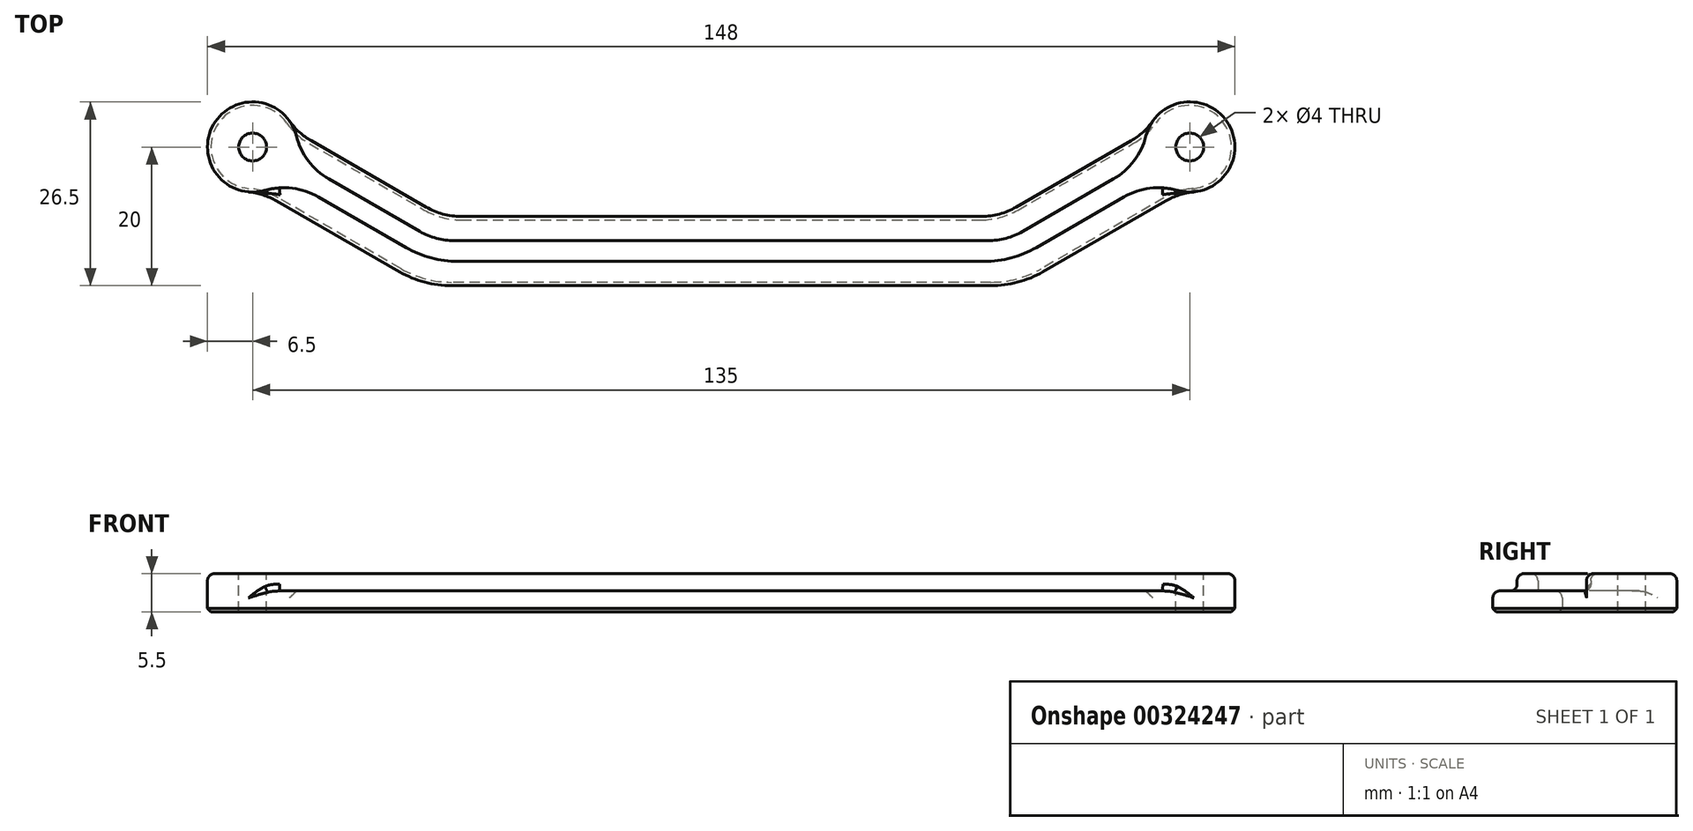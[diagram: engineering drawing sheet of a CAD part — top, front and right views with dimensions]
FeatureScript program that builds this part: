
annotation { "Feature Type Name" : "Feature", "Feature Type Description" : "" }
export const myFeature = defineFeature(function(context is Context, id is Id, definition is map)
    precondition{}
    {
        {
            var Q0;
            Q0=qCreatedBy(makeId("Top.planeOp"),FACE);
            var sketch = newSketch(context, id + "F0", { "sketchPlane" : qUnion([Q0])});
            skLineSegment(sketch, "E0", {"start": v(0, 0) * mm, "end": v(67.5, 0) * mm, "construction": true});
            skLineSegment(sketch, "E1", {"start": v(0, 0) * mm, "end": v(0, 13.51) * mm, "construction": true});
            skCircle(sketch, "E2", {"center": v(67.5, 0) * mm, "radius": 6.5 * mm});
            skCircle(sketch, "E3.MirrorC", {"center": v(-67.5, 0) * mm, "radius": 6.5 * mm});
            skSolve(sketch);
        }
        {
            var Q0;
            Q0=qSketchRegion(id+"F0",true);
            extrude(context, id + "F1", {"entities" : qUnion([Q0]), "depth" : 5.5 * mm});
        }
        {
            var Q0;
            Q0=qCreatedBy(makeId("Top.planeOp"),FACE);
            var sketch = newSketch(context, id + "F2", { "sketchPlane" : qUnion([Q0])});
            skLineSegment(sketch, "E4", {"start": v(-67.5, 0) * mm, "end": v(67.5, 0) * mm, "construction": true});
            skLineSegment(sketch, "E5", {"start": v(-67.5, 0) * mm, "end": v(-41.52, -15) * mm, "construction": true});
            skLineSegment(sketch, "E6", {"start": v(-41.52, -15) * mm, "end": v(0, -15) * mm, "construction": true});
            skLineSegment(sketch, "E7", {"start": v(0, -15) * mm, "end": v(0, 0) * mm, "construction": true});
            skLineSegment(sketch, "E8.MirrorCS", {"start": v(41.52, -15) * mm, "end": v(0, -15) * mm, "construction": true});
            skLineSegment(sketch, "E9.MirrorCS", {"start": v(67.5, 0) * mm, "end": v(41.52, -15) * mm, "construction": true});
            skLineSegment(sketch, "E10.0", {"start": v(70, -4.33) * mm, "end": v(42.86, -20) * mm});
            skLineSegment(sketch, "E10.1", {"start": v(42.86, -20) * mm, "end": v(0, -20) * mm});
            skLineSegment(sketch, "E10.2", {"start": v(-42.86, -20) * mm, "end": v(0, -20) * mm});
            skLineSegment(sketch, "E10.3", {"start": v(-70, -4.33) * mm, "end": v(-42.86, -20) * mm});
            skLineSegment(sketch, "E11.0", {"start": v(65, 4.33) * mm, "end": v(40.18, -10) * mm});
            skLineSegment(sketch, "E11.1", {"start": v(40.18, -10) * mm, "end": v(0, -10) * mm});
            skLineSegment(sketch, "E11.2", {"start": v(-40.18, -10) * mm, "end": v(0, -10) * mm});
            skLineSegment(sketch, "E11.3", {"start": v(-65, 4.33) * mm, "end": v(-40.18, -10) * mm});
            skLineSegment(sketch, "E12", {"start": v(-70, -4.33) * mm, "end": v(-65, 4.33) * mm});
            skLineSegment(sketch, "E13", {"start": v(65, 4.33) * mm, "end": v(70, -4.33) * mm});
            skSolve(sketch);
        }
        {
            var Q0;
            Q0=qSketchRegion(id+"F2",true);
            extrude(context, id + "F3", {"entities" : qUnion([Q0]), "operationType" : NewBodyOperationType.ADD, "depth" : 3 * mm});
        }
        {
            var Q0;
            Q0=makeQuery(id+"F3.opExtrude","CAP_FACE",FACE,{"disambiguationData":[OSD([sQuery(id+"F2.wireOp",EDGE,"E10.0"),sQuery(id+"F2.wireOp",EDGE,"E10.1"),sQuery(id+"F2.wireOp",EDGE,"E10.2"),sQuery(id+"F2.wireOp",EDGE,"E10.3"),sQuery(id+"F2.wireOp",EDGE,"E11.0"),sQuery(id+"F2.wireOp",EDGE,"E11.1"),sQuery(id+"F2.wireOp",EDGE,"E11.2"),sQuery(id+"F2.wireOp",EDGE,"E11.3"),sQuery(id+"F2.wireOp",EDGE,"E12"),sQuery(id+"F2.wireOp",EDGE,"E13")])],"isStart":false});
            var sketch = newSketch(context, id + "F4", { "sketchPlane" : qUnion([Q0])});
            skLineSegment(sketch, "E14.0", {"start": v(68.25, -1.3) * mm, "end": v(41.92, -16.5) * mm});
            skLineSegment(sketch, "E14.1", {"start": v(41.92, -16.5) * mm, "end": v(0, -16.5) * mm});
            skLineSegment(sketch, "E14.2", {"start": v(-41.92, -16.5) * mm, "end": v(0, -16.5) * mm});
            skLineSegment(sketch, "E14.3", {"start": v(-68.25, -1.3) * mm, "end": v(-41.92, -16.5) * mm});
            skLineSegment(sketch, "E15.0", {"start": v(66.75, 1.3) * mm, "end": v(41.12, -13.5) * mm});
            skLineSegment(sketch, "E15.1", {"start": v(41.12, -13.5) * mm, "end": v(0, -13.5) * mm});
            skLineSegment(sketch, "E15.2", {"start": v(-41.12, -13.5) * mm, "end": v(0, -13.5) * mm});
            skLineSegment(sketch, "E15.3", {"start": v(-66.75, 1.3) * mm, "end": v(-41.12, -13.5) * mm});
            skLineSegment(sketch, "E16", {"start": v(-68.25, -1.3) * mm, "end": v(-66.75, 1.3) * mm});
            skLineSegment(sketch, "E17", {"start": v(66.75, 1.3) * mm, "end": v(68.25, -1.3) * mm});
            skSolve(sketch);
        }
        {
            var Q0;
            Q0=qSketchRegion(id+"F4",true);
            var Q1;
            Q1=makeQuery(id+"F1.opExtrude","CAP_FACE",FACE,{"disambiguationData":[OSD([sQuery(id+"F0.wireOp",EDGE,"E3.MirrorC")])],"isStart":false});
            extrude(context, id + "F5", {"entities" : qUnion([Q0]), "operationType" : NewBodyOperationType.ADD, "endBound" : BoundingType.UP_TO_SURFACE, "endBoundEntityFace" : qUnion([Q1]), "depth" : 25 * mm});
        }
        {
            var Q0;
            Q0=makeQuery(id+"F5.boolean.opBoolean","MERGE",FACE,{"derivedFrom":[makeQuery(id+"F1.opExtrude","CAP_FACE",FACE,{"disambiguationData":[OSD([sQuery(id+"F0.wireOp",EDGE,"E2")])],"isStart":false}),makeQuery(id+"F1.opExtrude","CAP_FACE",FACE,{"disambiguationData":[OSD([sQuery(id+"F0.wireOp",EDGE,"E3.MirrorC")])],"isStart":false}),makeQuery(id+"F5.opExtrude","CAP_FACE",FACE,{"disambiguationData":[OSD([sQuery(id+"F4.wireOp",EDGE,"E14.0"),sQuery(id+"F4.wireOp",EDGE,"E14.1"),sQuery(id+"F4.wireOp",EDGE,"E14.2"),sQuery(id+"F4.wireOp",EDGE,"E14.3"),sQuery(id+"F4.wireOp",EDGE,"E15.0"),sQuery(id+"F4.wireOp",EDGE,"E15.1"),sQuery(id+"F4.wireOp",EDGE,"E15.2"),sQuery(id+"F4.wireOp",EDGE,"E15.3"),sQuery(id+"F4.wireOp",EDGE,"E16"),sQuery(id+"F4.wireOp",EDGE,"E17")])],"isStart":false})]});
            var sketch = newSketch(context, id + "F6", { "sketchPlane" : qUnion([Q0])});
            skCircle(sketch, "E18", {"center": v(-67.5, 0) * mm, "radius": 2 * mm});
            skCircle(sketch, "E19", {"center": v(67.5, 0) * mm, "radius": 2 * mm});
            skSolve(sketch);
        }
        {
            var Q0;
            Q0=qSketchRegion(id+"F6",true);
            extrude(context, id + "F7", {"entities" : qUnion([Q0]), "operationType" : NewBodyOperationType.REMOVE, "endBound" : BoundingType.THROUGH_ALL, "oppositeDirection" : true, "depth" : 25 * mm});
        }
        {
            var Q0;
            Q0=makeQuery(id+"F3.boolean.opBoolean","INTERSECT",EDGE,{"derivedFrom":[makeQuery(id+"F1.opExtrude","SWEPT_FACE",FACE,{"disambiguationData":[OSD([sQuery(id+"F0.wireOp",EDGE,"E3.MirrorC")])]}),makeQuery(id+"F3.opExtrude","SWEPT_FACE",FACE,{"disambiguationData":[OSD([sQuery(id+"F2.wireOp",EDGE,"E10.3")])]})]});
            var Q1;
            Q1=makeQuery(id+"F3.boolean.opBoolean","INTERSECT",EDGE,{"derivedFrom":[makeQuery(id+"F1.opExtrude","SWEPT_FACE",FACE,{"disambiguationData":[OSD([sQuery(id+"F0.wireOp",EDGE,"E2")])]}),makeQuery(id+"F3.opExtrude","SWEPT_FACE",FACE,{"disambiguationData":[OSD([sQuery(id+"F2.wireOp",EDGE,"E10.0")])]})]});
            var Q2;
            Q2=makeQuery(id+"F3.boolean.opBoolean","INTERSECT",EDGE,{"derivedFrom":[makeQuery(id+"F1.opExtrude","SWEPT_FACE",FACE,{"disambiguationData":[OSD([sQuery(id+"F0.wireOp",EDGE,"E3.MirrorC")])]}),makeQuery(id+"F3.opExtrude","SWEPT_FACE",FACE,{"disambiguationData":[OSD([sQuery(id+"F2.wireOp",EDGE,"E11.3")])]})]});
            var Q3;
            Q3=makeQuery(id+"F3.boolean.opBoolean","INTERSECT",EDGE,{"derivedFrom":[makeQuery(id+"F1.opExtrude","SWEPT_FACE",FACE,{"disambiguationData":[OSD([sQuery(id+"F0.wireOp",EDGE,"E2")])]}),makeQuery(id+"F3.opExtrude","SWEPT_FACE",FACE,{"disambiguationData":[OSD([sQuery(id+"F2.wireOp",EDGE,"E11.0")])]})]});
            fillet(context, id + "F8", {"entities" : qUnion([Q0, Q1, Q2, Q3]), "radius" : 10 * mm, "tangentPropagation" : true, "allowEdgeOverflow" : false});
        }
        {
            var Q0;
            Q0=makeQuery(id+"F5.boolean.opBoolean","INTERSECT",EDGE,{"derivedFrom":[makeQuery(id+"F1.opExtrude","SWEPT_FACE",FACE,{"disambiguationData":[OSD([sQuery(id+"F0.wireOp",EDGE,"E2")])]}),makeQuery(id+"F5.opExtrude","SWEPT_FACE",FACE,{"disambiguationData":[OSD([sQuery(id+"F4.wireOp",EDGE,"E15.0")])]})]});
            var Q1;
            Q1=makeQuery(id+"F3.opExtrude","SWEPT_EDGE",EDGE,{"disambiguationData":[OSD([sQuery(id+"F2.wireOp",EDGE,"E11.0"),sQuery(id+"F2.wireOp",EDGE,"E11.1")])]});
            var Q2;
            Q2=makeQuery(id+"F5.opExtrude","SWEPT_EDGE",EDGE,{"disambiguationData":[OSD([sQuery(id+"F4.wireOp",EDGE,"E15.0"),sQuery(id+"F4.wireOp",EDGE,"E15.1")])]});
            var Q3;
            Q3=makeQuery(id+"F5.opExtrude","SWEPT_EDGE",EDGE,{"disambiguationData":[OSD([sQuery(id+"F4.wireOp",EDGE,"E15.2"),sQuery(id+"F4.wireOp",EDGE,"E15.3")])]});
            var Q4;
            Q4=makeQuery(id+"F3.opExtrude","SWEPT_EDGE",EDGE,{"disambiguationData":[OSD([sQuery(id+"F2.wireOp",EDGE,"E11.2"),sQuery(id+"F2.wireOp",EDGE,"E11.3")])]});
            var Q5;
            Q5=makeQuery(id+"F5.boolean.opBoolean","INTERSECT",EDGE,{"derivedFrom":[makeQuery(id+"F1.opExtrude","SWEPT_FACE",FACE,{"disambiguationData":[OSD([sQuery(id+"F0.wireOp",EDGE,"E3.MirrorC")])]}),makeQuery(id+"F5.opExtrude","SWEPT_FACE",FACE,{"disambiguationData":[OSD([sQuery(id+"F4.wireOp",EDGE,"E15.3")])]})]});
            var Q6;
            Q6=makeQuery(id+"F5.boolean.opBoolean","INTERSECT",EDGE,{"derivedFrom":[makeQuery(id+"F1.opExtrude","SWEPT_FACE",FACE,{"disambiguationData":[OSD([sQuery(id+"F0.wireOp",EDGE,"E3.MirrorC")])]}),makeQuery(id+"F5.opExtrude","SWEPT_FACE",FACE,{"disambiguationData":[OSD([sQuery(id+"F4.wireOp",EDGE,"E14.3")])]})]});
            var Q7;
            Q7=makeQuery(id+"F5.boolean.opBoolean","INTERSECT",EDGE,{"derivedFrom":[makeQuery(id+"F1.opExtrude","SWEPT_FACE",FACE,{"disambiguationData":[OSD([sQuery(id+"F0.wireOp",EDGE,"E2")])]}),makeQuery(id+"F5.opExtrude","SWEPT_FACE",FACE,{"disambiguationData":[OSD([sQuery(id+"F4.wireOp",EDGE,"E14.0")])]})]});
            fillet(context, id + "F9", {"entities" : qUnion([Q0, Q1, Q2, Q3, Q4, Q5, Q6, Q7]), "radius" : 10 * mm, "tangentPropagation" : true, "allowEdgeOverflow" : false});
        }
        {
            var Q0;
            Q0=makeQuery(id+"F3.opExtrude","SWEPT_EDGE",EDGE,{"disambiguationData":[OSD([sQuery(id+"F2.wireOp",EDGE,"E10.0"),sQuery(id+"F2.wireOp",EDGE,"E10.1")])]});
            var Q1;
            Q1=makeQuery(id+"F5.opExtrude","SWEPT_EDGE",EDGE,{"disambiguationData":[OSD([sQuery(id+"F4.wireOp",EDGE,"E14.0"),sQuery(id+"F4.wireOp",EDGE,"E14.1")])]});
            var Q2;
            Q2=makeQuery(id+"F3.opExtrude","SWEPT_EDGE",EDGE,{"disambiguationData":[OSD([sQuery(id+"F2.wireOp",EDGE,"E10.2"),sQuery(id+"F2.wireOp",EDGE,"E10.3")])]});
            var Q3;
            Q3=makeQuery(id+"F5.opExtrude","SWEPT_EDGE",EDGE,{"disambiguationData":[OSD([sQuery(id+"F4.wireOp",EDGE,"E14.2"),sQuery(id+"F4.wireOp",EDGE,"E14.3")])]});
            fillet(context, id + "F10", {"entities" : qUnion([Q0, Q1, Q2, Q3]), "radius" : 15 * mm, "tangentPropagation" : true, "allowEdgeOverflow" : false});
        }
        {
            var Q0;
            Q0=makeQuery(id+"F3.opExtrude","CAP_EDGE",EDGE,{"disambiguationData":[OSD([sQuery(id+"F2.wireOp",EDGE,"E10.1"),sQuery(id+"F2.wireOp",EDGE,"E10.2")])],"isStart":false});
            var Q1;
            {var subQ0=sQuery(id+"F4.wireOp",EDGE,"E14.3");var subQ1=sQuery(id+"F4.wireOp",EDGE,"E14.2");Q1=makeQuery(id+"F10.opFillet","BLEND_EDGE",EDGE,{"blendedFrom":[makeQuery(id+"F5.opExtrude","SWEPT_EDGE",EDGE,{"disambiguationData":[OSD([subQ1,subQ0])]}),makeQuery(id+"F5.boolean.opBoolean","MERGE",FACE,{"derivedFrom":[makeQuery(id+"F1.opExtrude","CAP_FACE",FACE,{"disambiguationData":[OSD([sQuery(id+"F0.wireOp",EDGE,"E2")])],"isStart":false}),makeQuery(id+"F1.opExtrude","CAP_FACE",FACE,{"disambiguationData":[OSD([sQuery(id+"F0.wireOp",EDGE,"E3.MirrorC")])],"isStart":false}),makeQuery(id+"F5.opExtrude","CAP_FACE",FACE,{"disambiguationData":[OSD([sQuery(id+"F4.wireOp",EDGE,"E14.0"),sQuery(id+"F4.wireOp",EDGE,"E14.1"),subQ1,subQ0,sQuery(id+"F4.wireOp",EDGE,"E15.0"),sQuery(id+"F4.wireOp",EDGE,"E15.1"),sQuery(id+"F4.wireOp",EDGE,"E15.2"),sQuery(id+"F4.wireOp",EDGE,"E15.3"),sQuery(id+"F4.wireOp",EDGE,"E16"),sQuery(id+"F4.wireOp",EDGE,"E17")])],"isStart":false})]})],"blendedInto":[makeQuery(id+"F5.boolean.opBoolean","MERGE",FACE,{"derivedFrom":[makeQuery(id+"F1.opExtrude","CAP_FACE",FACE,{"disambiguationData":[OSD([sQuery(id+"F0.wireOp",EDGE,"E2")])],"isStart":false}),makeQuery(id+"F1.opExtrude","CAP_FACE",FACE,{"disambiguationData":[OSD([sQuery(id+"F0.wireOp",EDGE,"E3.MirrorC")])],"isStart":false}),makeQuery(id+"F5.opExtrude","CAP_FACE",FACE,{"disambiguationData":[OSD([sQuery(id+"F4.wireOp",EDGE,"E14.0"),sQuery(id+"F4.wireOp",EDGE,"E14.1"),subQ1,subQ0,sQuery(id+"F4.wireOp",EDGE,"E15.0"),sQuery(id+"F4.wireOp",EDGE,"E15.1"),sQuery(id+"F4.wireOp",EDGE,"E15.2"),sQuery(id+"F4.wireOp",EDGE,"E15.3"),sQuery(id+"F4.wireOp",EDGE,"E16"),sQuery(id+"F4.wireOp",EDGE,"E17")])],"isStart":false})]})]});}
            var Q2;
            Q2=makeQuery(id+"F3.opExtrude","CAP_EDGE",EDGE,{"disambiguationData":[OSD([sQuery(id+"F2.wireOp",EDGE,"E11.3")])],"isStart":false});
            fillet(context, id + "F11", {"entities" : qUnion([Q0, Q1, Q2]), "radius" : 1 * mm, "tangentPropagation" : true, "allowEdgeOverflow" : false});
        }
        {
            var Q0;
            Q0=makeQuery(id+"F3.opExtrude","CAP_EDGE",EDGE,{"disambiguationData":[OSD([sQuery(id+"F2.wireOp",EDGE,"E11.1"),sQuery(id+"F2.wireOp",EDGE,"E11.2")])],"isStart":true});
            chamfer(context, id + "F12", {"entities" : qUnion([Q0]), "width" : .5 * mm, "tangentPropagation" : true});
        }
        {
            var Q0;
            Q0=makeQuery(id+"F5.opExtrude","CAP_EDGE",EDGE,{"disambiguationData":[OSD([sQuery(id+"F4.wireOp",EDGE,"E15.1"),sQuery(id+"F4.wireOp",EDGE,"E15.2")])],"isStart":true});
            var Q1;
            Q1=makeQuery(id+"F5.opExtrude","CAP_EDGE",EDGE,{"disambiguationData":[OSD([sQuery(id+"F4.wireOp",EDGE,"E14.1"),sQuery(id+"F4.wireOp",EDGE,"E14.2")])],"isStart":true});
            fillet(context, id + "F13", {"entities" : qUnion([Q0, Q1]), "radius" : 1 * mm, "tangentPropagation" : true, "allowEdgeOverflow" : false});
        }
    });
